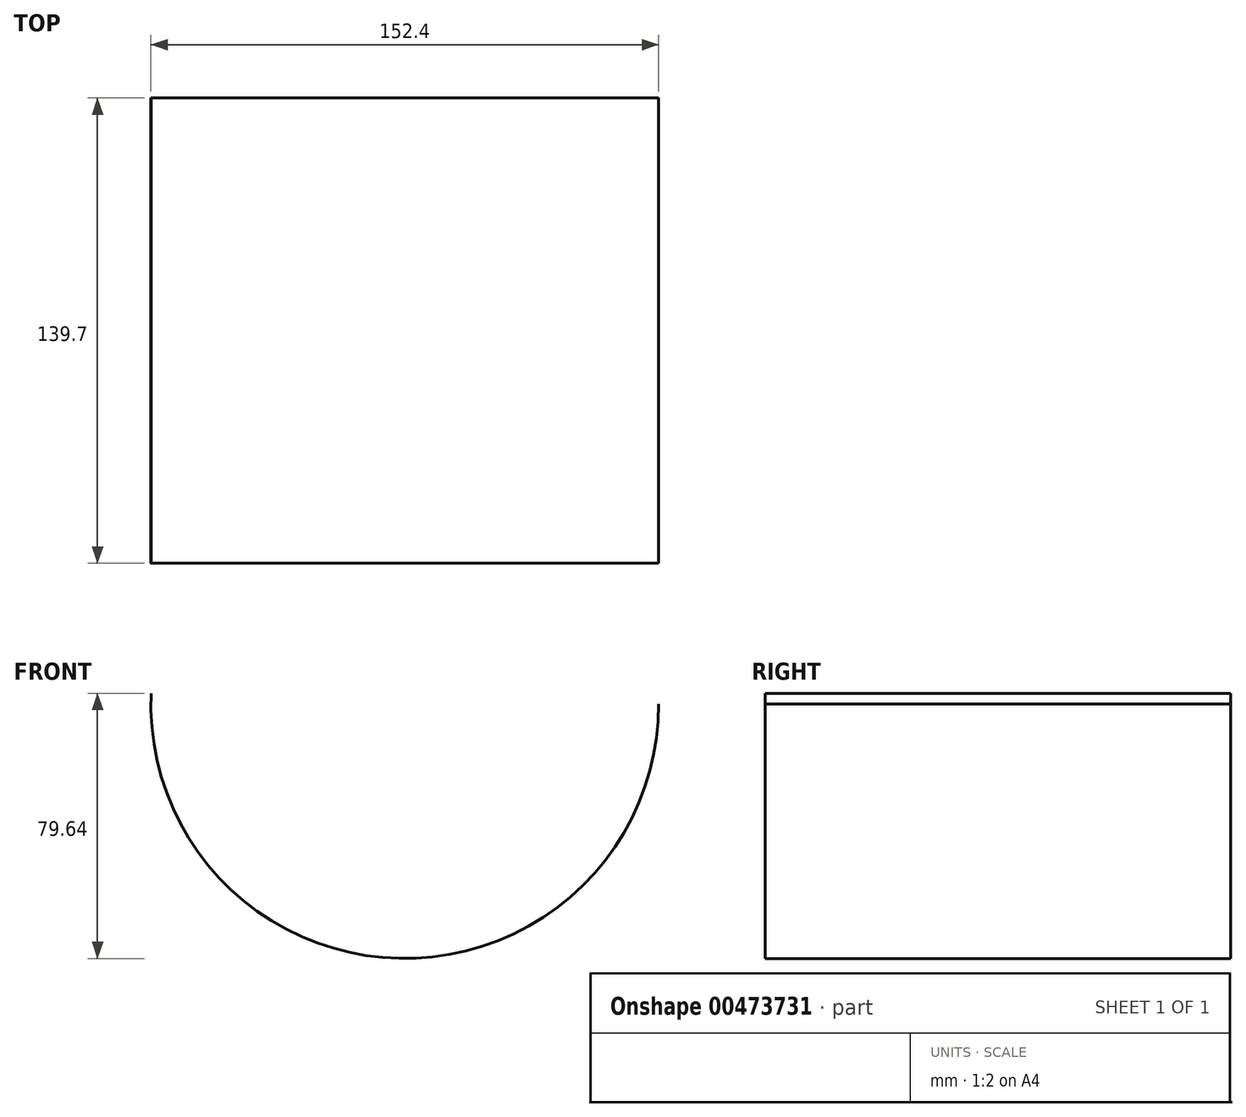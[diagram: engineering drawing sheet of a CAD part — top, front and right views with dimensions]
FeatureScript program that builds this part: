
annotation { "Feature Type Name" : "Feature", "Feature Type Description" : "" }
export const myFeature = defineFeature(function(context is Context, id is Id, definition is map)
    precondition{}
    {
        {
            var Q0;
            Q0=qCreatedBy(makeId("Front.planeOp"),FACE);
            var sketch = newSketch(context, id + "F0", { "sketchPlane" : qUnion([Q0])});
            skArc(sketch, "E0", {"start": v(-134.25, -19.4) * mm, "mid": v(-59.76, -99.02) * mm, "end": v(18.08, -22.67) * mm});
            skSolve(sketch);
        }
        {
            var Q0;
            Q0=sQuery(id+"F0.wireOp",EDGE,"E0");
            extrude(context, id + "F1", {"bodyType" : ToolBodyType.SURFACE, "surfaceEntities" : qUnion([Q0]), "depth" : 139.7 * mm});
        }
    });
